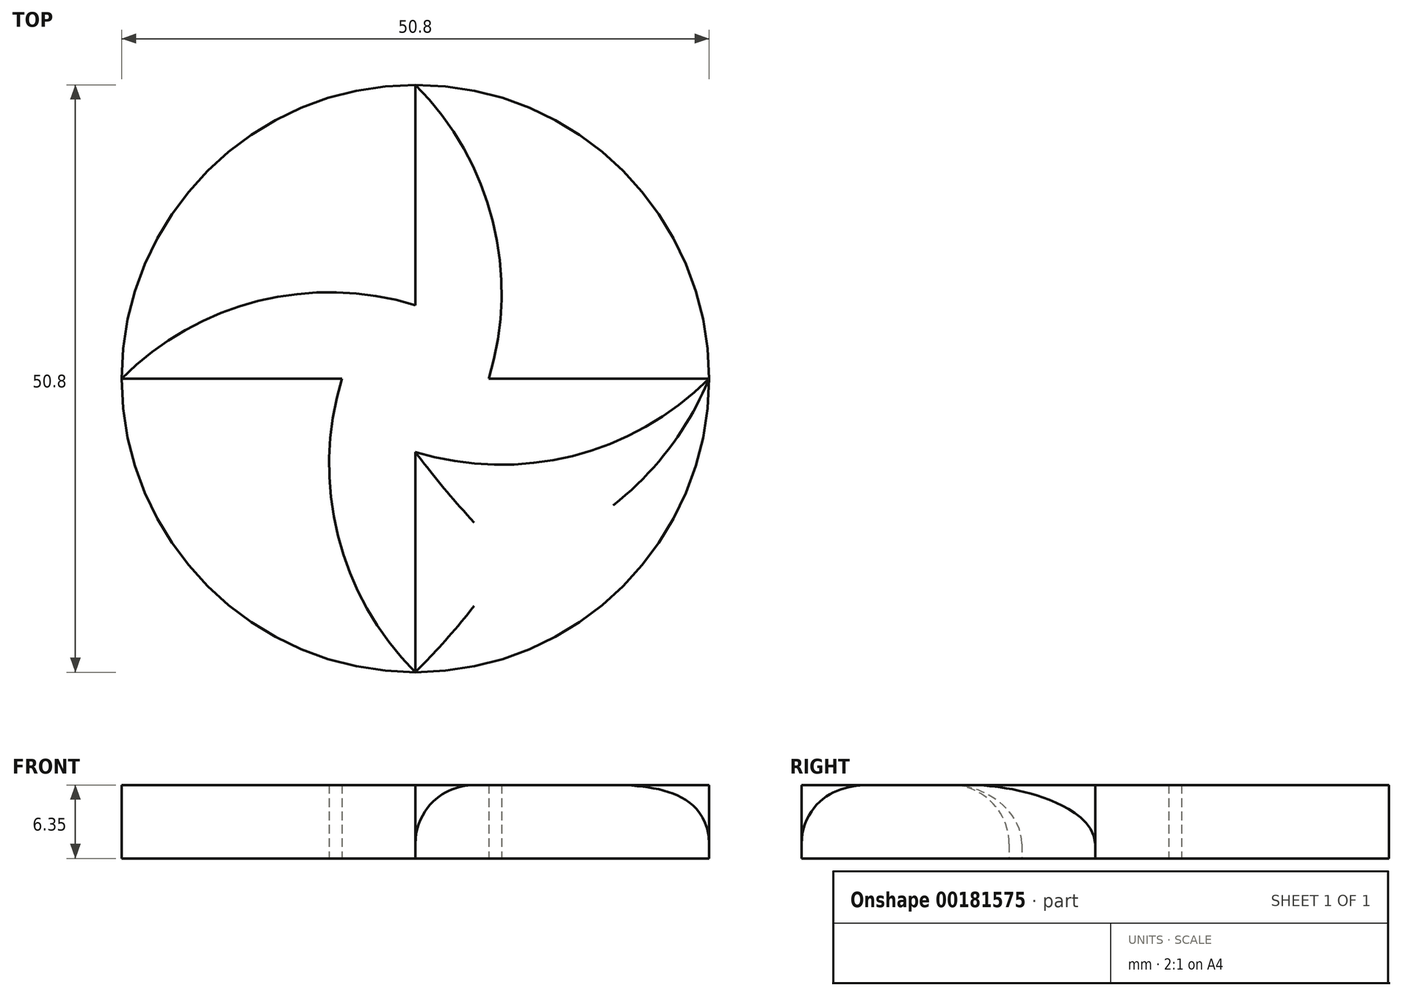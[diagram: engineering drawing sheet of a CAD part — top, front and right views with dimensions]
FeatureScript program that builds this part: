
annotation { "Feature Type Name" : "Feature", "Feature Type Description" : "" }
export const myFeature = defineFeature(function(context is Context, id is Id, definition is map)
    precondition{}
    {
        {
            var Q0;
            Q0=qCreatedBy(makeId("Top.planeOp"),FACE);
            var sketch = newSketch(context, id + "F0", { "sketchPlane" : qUnion([Q0])});
            skCircle(sketch, "E0", {"center": v(0, 0) * mm, "radius": 25.4 * mm});
            skCircle(sketch, "E1", {"center": v(0, 0) * mm, "radius": 6.35 * mm});
            skLineSegment(sketch, "E2", {"start": v(0, 0) * mm, "end": v(0, 6.35) * mm});
            skLineSegment(sketch, "E3", {"start": v(0, 0) * mm, "end": v(6.35, 0) * mm});
            skLineSegment(sketch, "E4", {"start": v(0, 0) * mm, "end": v(0, -6.35) * mm});
            skLineSegment(sketch, "E5", {"start": v(0, 0) * mm, "end": v(-6.35, 0) * mm});
            skLineSegment(sketch, "E6", {"start": v(0, 3.18) * mm, "end": v(0, 25.4) * mm});
            skLineSegment(sketch, "E7", {"start": v(3.18, 0) * mm, "end": v(25.4, 0) * mm});
            skLineSegment(sketch, "E8", {"start": v(0, -3.18) * mm, "end": v(0, -25.4) * mm});
            skLineSegment(sketch, "E9", {"start": v(-3.18, 0) * mm, "end": v(-25.4, 0) * mm});
            skArc(sketch, "E10", {"start": v(6.35, 0) * mm, "mid": v(6.7, 13.58) * mm, "end": v(0, 25.4) * mm});
            skArc(sketch, "E11", {"start": v(0, -6.35) * mm, "mid": v(13.58, -6.7) * mm, "end": v(25.4, 0) * mm});
            skArc(sketch, "E12", {"start": v(-6.35, 0) * mm, "mid": v(-6.7, -13.58) * mm, "end": v(0, -25.4) * mm});
            skArc(sketch, "E13", {"start": v(0, 6.35) * mm, "mid": v(-13.58, 6.7) * mm, "end": v(-25.4, 0) * mm});
            skSolve(sketch);
        }
        {
            var Q0;
            {var subQ0=sQuery(id+"F0.wireOp",EDGE,"E10");Q0=makeQuery(id+"F0.imprint","IMPRINT",FACE,{"disambiguationData":[TD([[makeQuery(id+"F0.imprint","IMPRINT",EDGE,{"derivedFrom":subQ0}),-1.0]])]});}
            var Q1;
            {var subQ3=sQuery(id+"F0.wireOp",EDGE,"E13");Q1=makeQuery(id+"F0.imprint","IMPRINT",FACE,{"disambiguationData":[TD([[makeQuery(id+"F0.imprint","IMPRINT",EDGE,{"derivedFrom":subQ3}),-1.0]])]});}
            var Q2;
            {var subQ0=sQuery(id+"F0.wireOp",EDGE,"E12");Q2=makeQuery(id+"F0.imprint","IMPRINT",FACE,{"disambiguationData":[TD([[makeQuery(id+"F0.imprint","IMPRINT",EDGE,{"derivedFrom":subQ0}),-1.0]])]});}
            var Q3;
            {var subQ0=sQuery(id+"F0.wireOp",EDGE,"E11");Q3=makeQuery(id+"F0.imprint","IMPRINT",FACE,{"disambiguationData":[TD([[makeQuery(id+"F0.imprint","IMPRINT",EDGE,{"derivedFrom":subQ0}),-1.0]])]});}
            extrude(context, id + "F1", {"entities" : qUnion([Q0, Q1, Q2, Q3]), "endBound" : BoundingType.SYMMETRIC, "depth" : 6.35 * mm});
        }
        {
            var Q0;
            Q0=makeQuery(id+"F1.opExtrude","CAP_FACE",FACE,{"disambiguationData":[OSD([sQuery(id+"F0.wireOp",EDGE,"E0"),sQuery(id+"F0.wireOp",EDGE,"E8"),sQuery(id+"F0.wireOp",EDGE,"E11")])],"isStart":false});
            fillet(context, id + "F2", {"entities" : qUnion([Q0]), "radius" : 5.08 * mm, "tangentPropagation" : true, "allowEdgeOverflow" : false});
        }
    });
